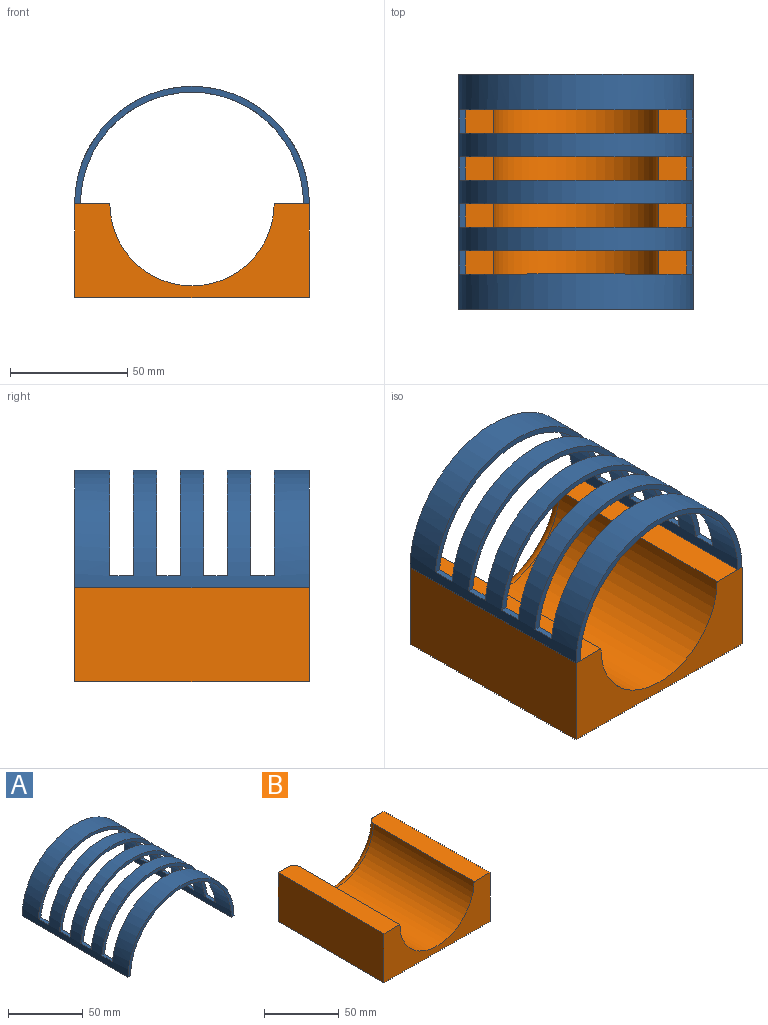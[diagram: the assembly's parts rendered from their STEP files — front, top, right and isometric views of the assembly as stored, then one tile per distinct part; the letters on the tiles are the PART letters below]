
ASSEMBLY  parts=2 mates=1
PART A: 22 faces, bbox 100x100x50 mm
  f0: plane 100x2.5mm, normal (0,0,-1), area 250mm2, adj f1,f3,f4,f5
  f1: cylinder r=50mm len=100mm, axis (0,1,0), area 9825.4mm2, adj f0,f2,f4,f5,f6,f7,f8,f9
  f2: plane 100x2.5mm, normal (0,0,-1), area 250mm2, adj f1,f3,f4,f5
  f3: cylinder r=47.5mm len=100mm, axis (0,1,0), area 9354.3mm2, adj f0,f2,f4,f5,f6,f7,f8,f9
  f4: plane 100x50mm, normal (0,-1,0), area 382.9mm2, adj f0,f1,f2,f3
  f5: plane 100x50mm, normal (0,1,0), area 382.9mm2, adj f0,f1,f2,f3
  f6: plane 99.5x45mm, normal (0,1,0), area 357.8mm2, adj f1,f3,f7,f8
  f7: plane 10x2.51mm, normal (0,0,1), area 25.1mm2, adj f1,f3,f6,f9
  f8: plane 10x2.51mm, normal (0,0,1), area 25.1mm2, adj f1,f3,f6,f9
  f9: plane 99.5x45mm, normal (0,-1,0), area 357.8mm2, adj f1,f3,f7,f8
  f10: plane 99.5x45mm, normal (0,1,0), area 357.8mm2, adj f1,f3,f11,f12
  f11: plane 10x2.51mm, normal (0,0,1), area 25.1mm2, adj f1,f3,f10,f13
  f12: plane 10x2.51mm, normal (0,0,1), area 25.1mm2, adj f1,f3,f10,f13
  f13: plane 99.5x45mm, normal (0,-1,0), area 357.8mm2, adj f1,f3,f11,f12
  f14: plane 99.5x45mm, normal (0,1,0), area 357.8mm2, adj f1,f3,f15,f16
  f15: plane 10x2.51mm, normal (0,0,1), area 25.1mm2, adj f1,f3,f14,f17
  f16: plane 10x2.51mm, normal (0,0,1), area 25.1mm2, adj f1,f3,f14,f17
  f17: plane 99.5x45mm, normal (0,-1,0), area 357.8mm2, adj f1,f3,f15,f16
  f18: plane 99.5x45mm, normal (0,-1,0), area 357.8mm2, adj f1,f3,f20,f21
  f19: plane 99.5x45mm, normal (0,1,0), area 357.8mm2, adj f1,f3,f20,f21
  f20: plane 10x2.51mm, normal (0,0,1), area 25.1mm2, adj f1,f3,f18,f19
  f21: plane 10x2.51mm, normal (0,0,1), area 25.1mm2, adj f1,f3,f18,f19
PART B: 10 faces, bbox 100x100x47.1 mm
  f0: plane 50x40mm, normal (0,1,0), area 743.4mm2, adj f1,f2,f3,f9
  f1: plane 100x15mm, normal (0,0,1), area 1494.6mm2, adj f0,f2,f6,f7,f9
  f2: plane 100x40mm, normal (-1,0,0), area 4000mm2, adj f0,f1,f3,f7
  f3: plane 100x100mm, normal (0,0,-1), area 10000mm2, adj f0,f2,f4,f7,f8
  f4: plane 100x40mm, normal (1,0,0), area 4000mm2, adj f3,f5,f7,f8
  f5: plane 100x15mm, normal (0,0,1), area 1494.6mm2, adj f4,f6,f7,f8,f9
  f6: cylinder r=35mm len=95mm, axis (0,1,0), area 10445.8mm2, adj f1,f5,f7,f9
  f7: plane 100x40mm, normal (0,-1,0), area 2075.8mm2, adj f1,f2,f3,f4,f5,f6
  f8: plane 50x40mm, normal (0,1,0), area 743.4mm2, adj f3,f4,f5,f9
  f9: torus R=40mm, axis (0,-1,0), area 908.4mm2, adj f0,f1,f5,f6,f8
PLACE A t=(-58.47,-14.97,37.35)mm
PLACE B t=(-58.47,-14.97,-2.65)mm
MATE fastened A.f2 <-> B.f1  axis (0,0,-1) through (-108.47,-14.97,37.35)mm
